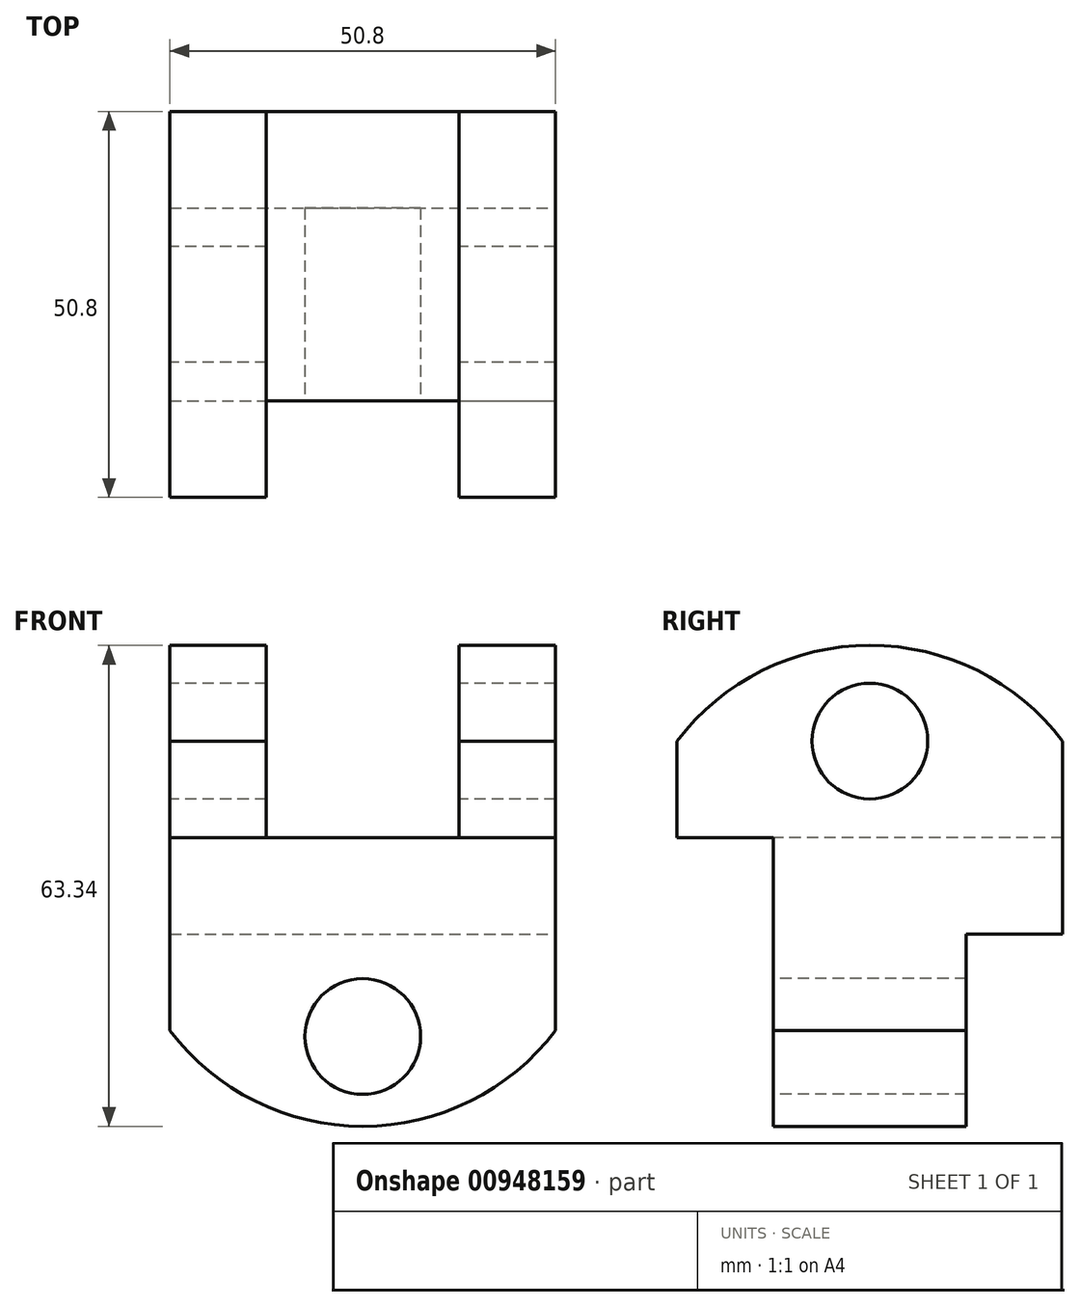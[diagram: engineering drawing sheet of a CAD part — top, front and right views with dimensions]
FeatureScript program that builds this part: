
annotation { "Feature Type Name" : "Feature", "Feature Type Description" : "" }
export const myFeature = defineFeature(function(context is Context, id is Id, definition is map)
    precondition{}
    {
        {
            var Q0;
            Q0=qCreatedBy(makeId("Top.planeOp"),FACE);
            var sketch = newSketch(context, id + "F0", { "sketchPlane" : qUnion([Q0])});
            skLineSegment(sketch, "E0.bottom", {"start": v(-39.7, 22.9) * mm, "end": v(11.1, 22.9) * mm});
            skLineSegment(sketch, "E0.top", {"start": v(-39.7, -27.9) * mm, "end": v(11.1, -27.9) * mm});
            skLineSegment(sketch, "E0.left", {"start": v(-39.7, 22.9) * mm, "end": v(-39.7, -27.9) * mm});
            skLineSegment(sketch, "E0.right", {"start": v(11.1, 22.9) * mm, "end": v(11.1, -27.9) * mm});
            skLineSegment(sketch, "E1.bottom", {"start": v(-27, -27.9) * mm, "end": v(-1.6, -27.9) * mm});
            skLineSegment(sketch, "E1.top", {"start": v(-27, 22.9) * mm, "end": v(-1.6, 22.9) * mm});
            skLineSegment(sketch, "E2.bottom", {"start": v(-39.7, -15.2) * mm, "end": v(11.1, -15.2) * mm});
            skLineSegment(sketch, "E2.top", {"start": v(-39.7, 10.2) * mm, "end": v(11.1, 10.2) * mm});
            skLineSegment(sketch, "E2.left", {"start": v(-39.7, -15.2) * mm, "end": v(-39.7, 10.2) * mm});
            skLineSegment(sketch, "E2.right", {"start": v(11.1, -15.2) * mm, "end": v(11.1, 10.2) * mm});
            skSolve(sketch);
        }
        {
            var Q0;
            Q0=makeQuery(id+"F0.imprint","IMPRINT",FACE,{"disambiguationData":[TD([[makeQuery(id+"F0.imprint","IMPRINT",EDGE,{"derivedFrom":sQuery(id+"F0.wireOp",EDGE,"E0.bottom")}),-1.0]])]});
            var Q1;
            Q1=makeQuery(id+"F0.imprint","IMPRINT",FACE,{"disambiguationData":[TD([[makeQuery(id+"F0.imprint","IMPRINT",EDGE,{"derivedFrom":sQuery(id+"F0.wireOp",EDGE,"E1.bottom")}),1.0]])]});
            var Q2;
            Q2=makeQuery(id+"F0.imprint","IMPRINT",FACE,{"disambiguationData":[TD([[makeQuery(id+"F0.imprint","IMPRINT",EDGE,{"derivedFrom":sQuery(id+"F0.wireOp",EDGE,"E2.bottom")}),1.0]])]});
            extrude(context, id + "F1", {"entities" : qUnion([Q0, Q1, Q2]), "depth" : 12.7 * mm, "offsetDistance" : 25.4 * mm});
        }
        {
            var Q0;
            Q0=makeQuery(id+"F1.opExtrude","CAP_FACE",FACE,{"disambiguationData":[OSD([sQuery(id+"F0.wireOp",EDGE,"E0.bottom"),sQuery(id+"F0.wireOp",EDGE,"E0.top"),sQuery(id+"F0.wireOp",EDGE,"E0.left"),sQuery(id+"F0.wireOp",EDGE,"E0.right")])],"isStart":false});
            var sketch = newSketch(context, id + "F2", { "sketchPlane" : qUnion([Q0])});
            skLineSegment(sketch, "E3.bottom", {"start": v(-39.7, 22.9) * mm, "end": v(-27, 22.9) * mm});
            skLineSegment(sketch, "E3.top", {"start": v(-39.7, -27.9) * mm, "end": v(-27, -27.9) * mm});
            skLineSegment(sketch, "E3.left", {"start": v(-39.7, 22.9) * mm, "end": v(-39.7, -27.9) * mm});
            skLineSegment(sketch, "E3.right", {"start": v(-27, 22.9) * mm, "end": v(-27, -27.9) * mm});
            skLineSegment(sketch, "E4.bottom", {"start": v(11.1, 22.9) * mm, "end": v(-1.6, 22.9) * mm});
            skLineSegment(sketch, "E4.top", {"start": v(11.1, -27.9) * mm, "end": v(-1.6, -27.9) * mm});
            skLineSegment(sketch, "E4.left", {"start": v(11.1, 22.9) * mm, "end": v(11.1, -27.9) * mm});
            skLineSegment(sketch, "E4.right", {"start": v(-1.6, 22.9) * mm, "end": v(-1.6, -27.9) * mm});
            skSolve(sketch);
        }
        {
            var Q0;
            Q0 = qSketchRegion(id + "F2", true);
            extrude(context, id + "F3", {"entities" : qUnion([Q0]), "operationType" : NewBodyOperationType.ADD, "depth" : 25.4 * mm, "offsetDistance" : 25.4 * mm});
        }
        {
            var Q0;
            Q0=makeQuery(id+"F3.boolean.opBoolean","MERGE",FACE,{"derivedFrom":[makeQuery(id+"F1.opExtrude","SWEPT_FACE",FACE,{"disambiguationData":[OSD([sQuery(id+"F0.wireOp",EDGE,"E0.left")])]}),makeQuery(id+"F3.opExtrude","SWEPT_FACE",FACE,{"disambiguationData":[OSD([sQuery(id+"F2.wireOp",EDGE,"E3.left")])]})]});
            var sketch = newSketch(context, id + "F4", { "sketchPlane" : qUnion([Q0])});
            skCircle(sketch, "E5", {"center": v(2.5, 25.4) * mm, "radius": 7.62 * mm});
            skPoint(sketch, "E5.centerSnap0", {"position": v(2.5, 38.1) * mm});
            skArc(sketch, "E6", {"start": v(27.9, 25.4) * mm, "mid": v(2.5, 38.01) * mm, "end": v(-22.9, 25.4) * mm});
            skSolve(sketch);
        }
        {
            var Q0;
            {var subQ0=sQuery(id+"F4.wireOp",EDGE,"E6");Q0=makeQuery(id+"F4.imprint","IMPRINT",FACE,{"disambiguationData":[TD([[makeQuery(id+"F4.imprint","IMPRINT",EDGE,{"derivedFrom":subQ0}),-1.0]])]});}
            var Q1;
            Q1=makeQuery(id+"F4.imprint","IMPRINT",FACE,{"disambiguationData":[TD([[makeQuery(id+"F4.imprint","IMPRINT",EDGE,{"derivedFrom":sQuery(id+"F4.wireOp",EDGE,"E5")}),1.0]])]});
            extrude(context, id + "F5", {"entities" : qUnion([Q0, Q1]), "operationType" : NewBodyOperationType.REMOVE, "oppositeDirection" : true, "depth" : 53.34 * mm, "offsetDistance" : 25.4 * mm});
        }
        {
            var Q0;
            Q0=makeQuery(id+"F0.imprint","IMPRINT",FACE,{"disambiguationData":[TD([[makeQuery(id+"F0.imprint","IMPRINT",EDGE,{"derivedFrom":sQuery(id+"F0.wireOp",EDGE,"E2.bottom")}),1.0]])]});
            extrude(context, id + "F6", {"entities" : qUnion([Q0]), "operationType" : NewBodyOperationType.ADD, "oppositeDirection" : true, "depth" : 25.4 * mm, "offsetDistance" : 25.4 * mm});
        }
        {
            var Q0;
            Q0=makeQuery(id+"F6.opExtrude","SWEPT_FACE",FACE,{"disambiguationData":[OSD([sQuery(id+"F0.wireOp",EDGE,"E2.bottom")])]});
            var sketch = newSketch(context, id + "F7", { "sketchPlane" : qUnion([Q0])});
            skArc(sketch, "E7", {"start": v(-39.7, -12.7) * mm, "mid": v(-14.3, -25.33) * mm, "end": v(11.1, -12.7) * mm});
            skCircle(sketch, "E8", {"center": v(-14.3, -13.5) * mm, "radius": 7.62 * mm});
            skPoint(sketch, "E8.centerSnap0", {"position": v(-14.3, -25.4) * mm});
            skSolve(sketch);
        }
        {
            var Q0;
            Q0=makeQuery(id+"F7.imprint","IMPRINT",FACE,{"disambiguationData":[TD([[makeQuery(id+"F7.imprint","IMPRINT",EDGE,{"derivedFrom":sQuery(id+"F7.wireOp",EDGE,"E8")}),1.0]])]});
            var Q1;
            {var subQ0=sQuery(id+"F7.wireOp",EDGE,"E7");Q1=makeQuery(id+"F7.imprint","IMPRINT",FACE,{"disambiguationData":[TD([[makeQuery(id+"F7.imprint","IMPRINT",EDGE,{"derivedFrom":subQ0}),-1.0]])]});}
            extrude(context, id + "F8", {"entities" : qUnion([Q0, Q1]), "operationType" : NewBodyOperationType.REMOVE, "oppositeDirection" : true, "depth" : 25.4 * mm, "offsetDistance" : 25.4 * mm});
        }
    });
